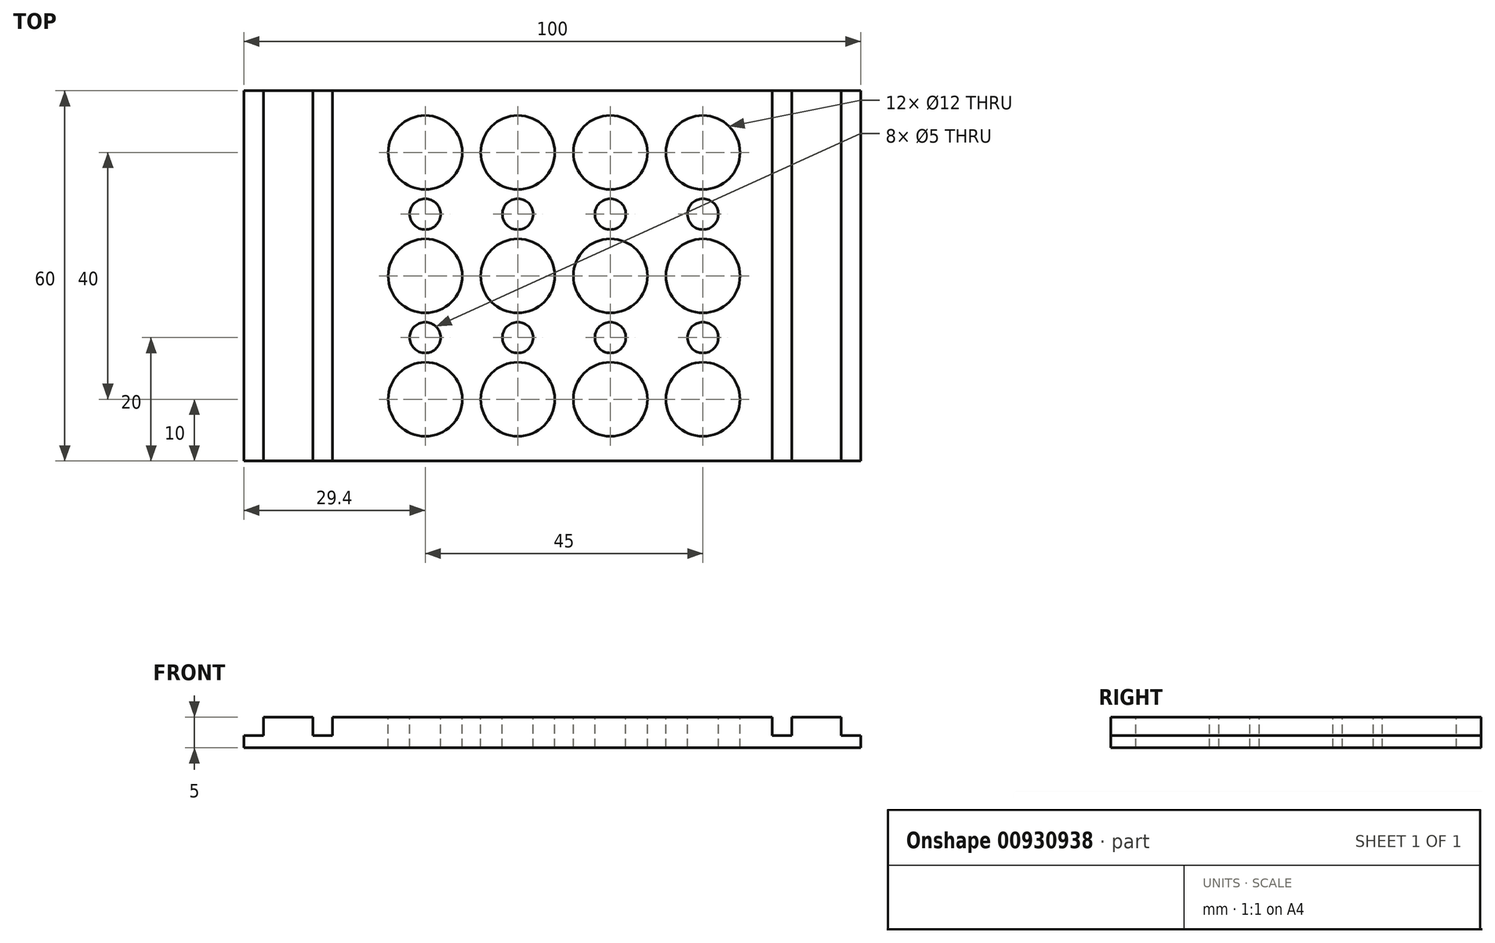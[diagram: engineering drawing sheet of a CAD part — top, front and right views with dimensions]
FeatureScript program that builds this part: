
annotation { "Feature Type Name" : "Feature", "Feature Type Description" : "" }
export const myFeature = defineFeature(function(context is Context, id is Id, definition is map)
    precondition{}
    {
        {
            var Q0;
            Q0=qCreatedBy(makeId("Top.planeOp"),FACE);
            var sketch = newSketch(context, id + "F0", { "sketchPlane" : qUnion([Q0])});
            skLineSegment(sketch, "E0.bottom", {"start": v(0, -60) * mm, "end": v(100, -60) * mm});
            skLineSegment(sketch, "E0.top", {"start": v(0, 0) * mm, "end": v(100, 0) * mm});
            skLineSegment(sketch, "E0.left", {"start": v(0, -60) * mm, "end": v(0, 0) * mm});
            skLineSegment(sketch, "E0.right", {"start": v(100, -60) * mm, "end": v(100, 0) * mm});
            skSolve(sketch);
        }
        {
            var Q0;
            Q0=qSketchRegion(id+"F0",true);
            extrude(context, id + "F1", {"entities" : qUnion([Q0]), "oppositeDirection" : true, "depth" : 5 * mm, "offsetDistance" : 25 * mm});
        }
        {
            var Q0;
            Q0=makeQuery(id+"F1.opExtrude","CAP_FACE",FACE,{"disambiguationData":[OSD([sQuery(id+"F0.wireOp",EDGE,"E0.bottom"),sQuery(id+"F0.wireOp",EDGE,"E0.top"),sQuery(id+"F0.wireOp",EDGE,"E0.left"),sQuery(id+"F0.wireOp",EDGE,"E0.right")])],"isStart":true});
            var sketch = newSketch(context, id + "F2", { "sketchPlane" : qUnion([Q0])});
            skLineSegment(sketch, "E1", {"start": v(100, 0) * mm, "end": v(100, -60) * mm});
            skLineSegment(sketch, "E2", {"start": v(100, -60) * mm, "end": v(96.8, -60) * mm});
            skLineSegment(sketch, "E3", {"start": v(96.8, -60) * mm, "end": v(96.8, 0) * mm});
            skLineSegment(sketch, "E4", {"start": v(96.8, 0) * mm, "end": v(100, 0) * mm});
            skLineSegment(sketch, "E5", {"start": v(88.8, 0) * mm, "end": v(88.8, -60) * mm});
            skLineSegment(sketch, "E6", {"start": v(88.8, -60) * mm, "end": v(85.6, -60) * mm});
            skLineSegment(sketch, "E7", {"start": v(85.6, -60) * mm, "end": v(85.6, 0) * mm});
            skLineSegment(sketch, "E8", {"start": v(85.6, 0) * mm, "end": v(88.8, 0) * mm});
            skLineSegment(sketch, "E9", {"start": v(0, -60) * mm, "end": v(3.2, -60) * mm});
            skLineSegment(sketch, "E10", {"start": v(11.2, -60) * mm, "end": v(14.4, -60) * mm});
            skLineSegment(sketch, "E11", {"start": v(0, -60) * mm, "end": v(0, 0) * mm});
            skLineSegment(sketch, "E12", {"start": v(0, 0) * mm, "end": v(3.2, 0) * mm});
            skLineSegment(sketch, "E13", {"start": v(3.2, 0) * mm, "end": v(3.2, -60) * mm});
            skLineSegment(sketch, "E14", {"start": v(11.2, -60) * mm, "end": v(11.2, 0) * mm});
            skLineSegment(sketch, "E15", {"start": v(11.2, 0) * mm, "end": v(14.4, 0) * mm});
            skLineSegment(sketch, "E16", {"start": v(14.4, 0) * mm, "end": v(14.4, -60) * mm});
            skSolve(sketch);
        }
        {
            var Q0;
            Q0=makeQuery(id+"F2.imprint","IMPRINT",FACE,{"disambiguationData":[TD([[makeQuery(id+"F2.imprint","IMPRINT",EDGE,{"derivedFrom":sQuery(id+"F2.wireOp",EDGE,"E9")}),1.0]])]});
            var Q1;
            Q1=makeQuery(id+"F2.imprint","IMPRINT",FACE,{"disambiguationData":[TD([[makeQuery(id+"F2.imprint","IMPRINT",EDGE,{"derivedFrom":sQuery(id+"F2.wireOp",EDGE,"E10")}),1.0]])]});
            var Q2;
            Q2=makeQuery(id+"F2.imprint","IMPRINT",FACE,{"disambiguationData":[TD([[makeQuery(id+"F2.imprint","IMPRINT",EDGE,{"derivedFrom":sQuery(id+"F2.wireOp",EDGE,"E5")}),-1.0]])]});
            var Q3;
            Q3=makeQuery(id+"F2.imprint","IMPRINT",FACE,{"disambiguationData":[TD([[makeQuery(id+"F2.imprint","IMPRINT",EDGE,{"derivedFrom":sQuery(id+"F2.wireOp",EDGE,"E1")}),1.0]])]});
            extrude(context, id + "F3", {"entities" : qUnion([Q0, Q1, Q2, Q3]), "operationType" : NewBodyOperationType.REMOVE, "oppositeDirection" : true, "depth" : 3 * mm, "offsetDistance" : 25 * mm});
        }
        {
            var Q0;
            {var subQ0=sQuery(id+"F0.wireOp",EDGE,"E0.bottom");var subQ1=sQuery(id+"F0.wireOp",EDGE,"E0.top");Q0=makeQuery(id+"F3.boolean.opBoolean","SPLIT",FACE,{"disambiguationData":[TD([makeQuery(id+"F3.opExtrude","SWEPT_FACE",FACE,{"disambiguationData":[OSD([sQuery(id+"F2.wireOp",EDGE,"E7")])]})])],"derivedFrom":makeQuery(id+"F1.opExtrude","CAP_FACE",FACE,{"disambiguationData":[OSD([subQ0,subQ1,sQuery(id+"F0.wireOp",EDGE,"E0.left"),sQuery(id+"F0.wireOp",EDGE,"E0.right")])],"isStart":true})});}
            var sketch = newSketch(context, id + "F4", { "sketchPlane" : qUnion([Q0])});
            skCircle(sketch, "E17", {"center": v(29.4, -50) * mm, "radius": 6 * mm});
            skCircle(sketch, "E18", {"center": v(44.4, -50) * mm, "radius": 6 * mm});
            skCircle(sketch, "E19", {"center": v(59.4, -50) * mm, "radius": 6 * mm});
            skCircle(sketch, "E20", {"center": v(74.4, -50) * mm, "radius": 6 * mm});
            skCircle(sketch, "E21", {"center": v(74.4, -40) * mm, "radius": 2.5 * mm});
            skCircle(sketch, "E22", {"center": v(59.4, -40) * mm, "radius": 2.5 * mm});
            skCircle(sketch, "E23", {"center": v(44.4, -40) * mm, "radius": 2.5 * mm});
            skCircle(sketch, "E24", {"center": v(29.4, -40) * mm, "radius": 2.5 * mm});
            skCircle(sketch, "E25", {"center": v(29.4, -30) * mm, "radius": 6 * mm});
            skCircle(sketch, "E26", {"center": v(44.4, -30) * mm, "radius": 6 * mm});
            skCircle(sketch, "E27", {"center": v(59.4, -30) * mm, "radius": 6 * mm});
            skCircle(sketch, "E28", {"center": v(74.4, -30) * mm, "radius": 6 * mm});
            skCircle(sketch, "E29", {"center": v(74.4, -20) * mm, "radius": 2.5 * mm});
            skCircle(sketch, "E30", {"center": v(59.4, -20) * mm, "radius": 2.5 * mm});
            skCircle(sketch, "E31", {"center": v(44.4, -20) * mm, "radius": 2.5 * mm});
            skCircle(sketch, "E32", {"center": v(29.4, -20) * mm, "radius": 2.5 * mm});
            skCircle(sketch, "E33", {"center": v(74.4, -10) * mm, "radius": 6 * mm});
            skCircle(sketch, "E34", {"center": v(59.4, -10) * mm, "radius": 6 * mm});
            skCircle(sketch, "E35", {"center": v(44.4, -10) * mm, "radius": 6 * mm});
            skCircle(sketch, "E36", {"center": v(29.4, -10) * mm, "radius": 6 * mm});
            skSolve(sketch);
        }
        {
            var Q0;
            Q0 = qSketchRegion(id + "F4", true);
            extrude(context, id + "F5", {"entities" : qUnion([Q0]), "operationType" : NewBodyOperationType.REMOVE, "oppositeDirection" : true, "depth" : 5 * mm, "offsetDistance" : 25 * mm});
        }
    });
